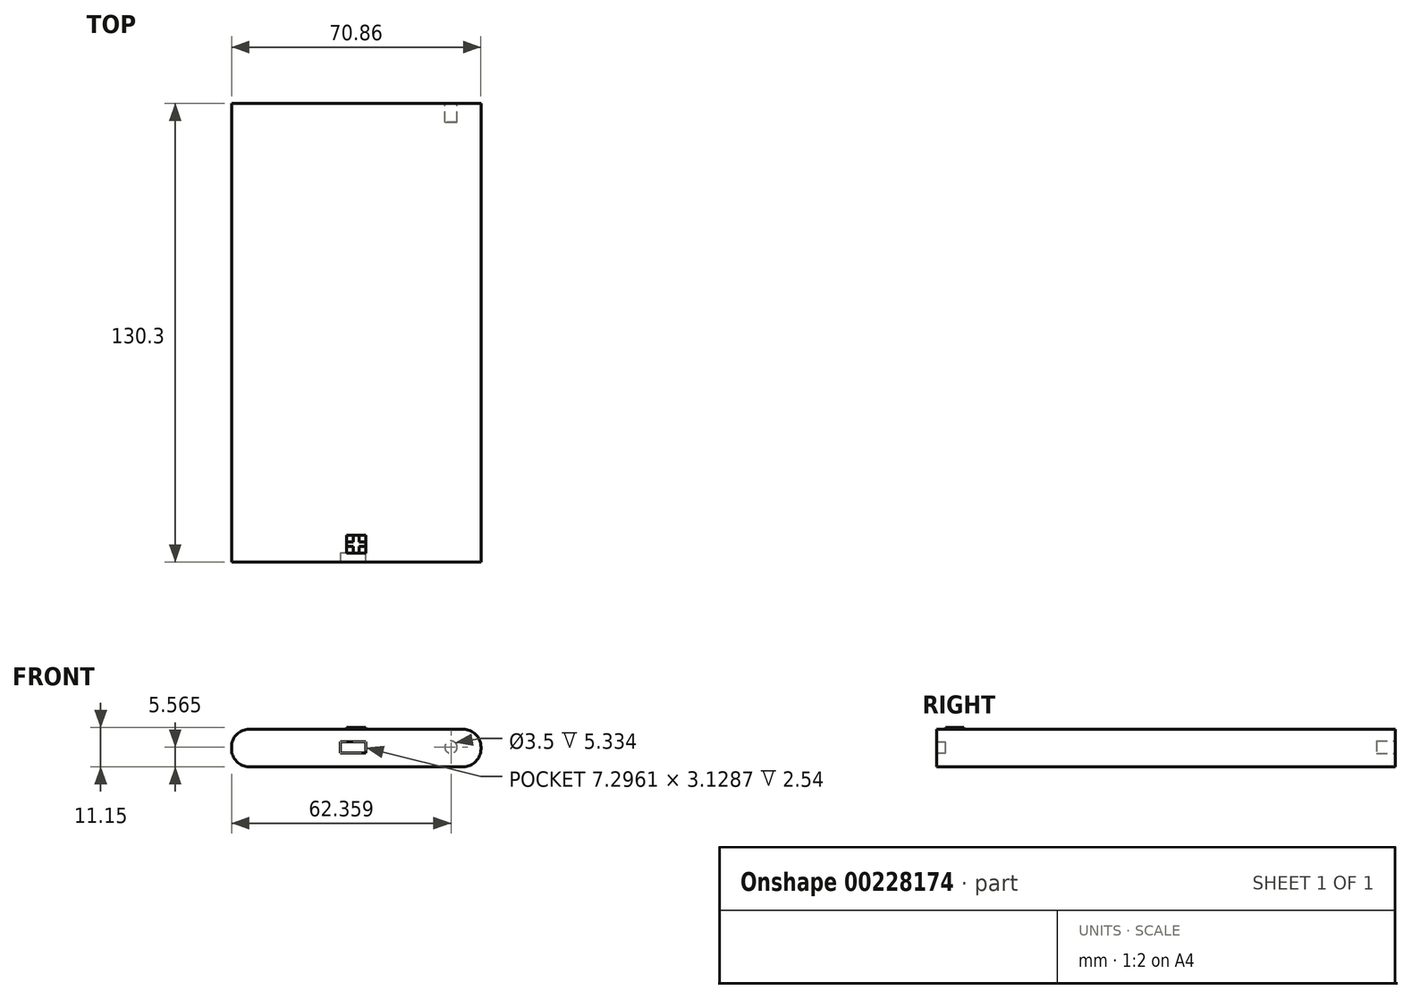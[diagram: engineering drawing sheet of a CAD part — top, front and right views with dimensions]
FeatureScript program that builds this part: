
annotation { "Feature Type Name" : "Feature", "Feature Type Description" : "" }
export const myFeature = defineFeature(function(context is Context, id is Id, definition is map)
    precondition{}
    {
        {
            var Q0;
            Q0=qCreatedBy(makeId("Top.planeOp"),FACE);
            var sketch = newSketch(context, id + "F0", { "sketchPlane" : qUnion([Q0])});
            skLineSegment(sketch, "E0.bottom", {"start": v(-84.07, 53.94) * mm, "end": v(-13.2, 53.94) * mm});
            skLineSegment(sketch, "E0.top", {"start": v(-84.07, -76.36) * mm, "end": v(-13.2, -76.36) * mm});
            skLineSegment(sketch, "E0.left", {"start": v(-84.07, 53.94) * mm, "end": v(-84.07, -76.36) * mm});
            skLineSegment(sketch, "E0.right", {"start": v(-13.2, 53.94) * mm, "end": v(-13.2, -76.36) * mm});
            skSolve(sketch);
        }
        {
            var Q0;
            Q0=makeQuery(id+"F0.imprint","IMPRINT",FACE,{"disambiguationData":[TD([[makeQuery(id+"F0.imprint","IMPRINT",EDGE,{"derivedFrom":sQuery(id+"F0.wireOp",EDGE,"E0.bottom")}),-1.0]])]});
            extrude(context, id + "F1", {"entities" : qUnion([Q0]), "depth" : 10.67 * mm});
        }
        {
            var Q0;
            Q0=makeQuery(id+"F1.opExtrude","CAP_EDGE",EDGE,{"disambiguationData":[OSD([sQuery(id+"F0.wireOp",EDGE,"E0.right")])],"isStart":false});
            var Q1;
            Q1=makeQuery(id+"F1.opExtrude","CAP_EDGE",EDGE,{"disambiguationData":[OSD([sQuery(id+"F0.wireOp",EDGE,"E0.right")])],"isStart":true});
            var Q2;
            Q2=makeQuery(id+"F1.opExtrude","CAP_EDGE",EDGE,{"disambiguationData":[OSD([sQuery(id+"F0.wireOp",EDGE,"E0.left")])],"isStart":true});
            var Q3;
            Q3=makeQuery(id+"F1.opExtrude","CAP_EDGE",EDGE,{"disambiguationData":[OSD([sQuery(id+"F0.wireOp",EDGE,"E0.left")])],"isStart":false});
            fillet(context, id + "F2", {"entities" : qUnion([Q0, Q1, Q2, Q3]), "radius" : 5.08 * mm, "tangentPropagation" : true, "allowEdgeOverflow" : false});
        }
        {
            var Q0;
            Q0=makeQuery(id+"F1.opExtrude","SWEPT_FACE",FACE,{"disambiguationData":[OSD([sQuery(id+"F0.wireOp",EDGE,"E0.top")])]});
            var sketch = newSketch(context, id + "F3", { "sketchPlane" : qUnion([Q0])});
            skLineSegment(sketch, "E1", {"start": v(-84.07, 5.59) * mm, "end": v(-9.23, 4.95) * mm, "construction": true});
            skLineSegment(sketch, "E2", {"start": v(-48.59, 5.28) * mm, "end": v(-48.68, -4.71) * mm});
            skLineSegment(sketch, "E3", {"start": v(-48.59, 5.28) * mm, "end": v(-48.59, 20.94) * mm});
            skLineSegment(sketch, "E4.bottom", {"start": v(-49.62, 7.04) * mm, "end": v(-53.17, 7.04) * mm});
            skLineSegment(sketch, "E4.top", {"start": v(-49.62, 3.9) * mm, "end": v(-53.17, 3.9) * mm});
            skLineSegment(sketch, "E4.left", {"start": v(-49.62, 7.04) * mm, "end": v(-49.62, 3.9) * mm});
            skLineSegment(sketch, "E4.right", {"start": v(-53.17, 7.04) * mm, "end": v(-53.17, 3.9) * mm});
            skLineSegment(sketch, "E5.MirrorCS", {"start": v(-48.59, 5.28) * mm, "end": v(-48.5, -4.71) * mm});
            skLineSegment(sketch, "E6.MirrorCS", {"start": v(-47.56, 7.04) * mm, "end": v(-47.56, 3.9) * mm});
            skLineSegment(sketch, "E7.MirrorCS", {"start": v(-47.56, 7.04) * mm, "end": v(-44, 7.04) * mm});
            skLineSegment(sketch, "E8.MirrorCS", {"start": v(-44, 7.04) * mm, "end": v(-44, 3.9) * mm});
            skLineSegment(sketch, "E9.MirrorCS", {"start": v(-47.56, 3.9) * mm, "end": v(-44, 3.9) * mm});
            skSolve(sketch);
        }
        {
            var Q0;
            Q0=makeQuery(id+"F3.imprint","IMPRINT",FACE,{"disambiguationData":[TD([[makeQuery(id+"F3.imprint","IMPRINT",EDGE,{"derivedFrom":sQuery(id+"F3.wireOp",EDGE,"E4.bottom")}),1.0]])]});
            var Q1;
            Q1=makeQuery(id+"F3.imprint","IMPRINT",FACE,{"disambiguationData":[TD([[makeQuery(id+"F3.imprint","IMPRINT",EDGE,{"derivedFrom":sQuery(id+"F3.wireOp",EDGE,"E6.MirrorCS")}),1.0]])]});
            extrude(context, id + "F4", {"entities" : qUnion([Q0, Q1]), "operationType" : NewBodyOperationType.REMOVE, "oppositeDirection" : true, "depth" : 2.54 * mm});
        }
        {
            var Q0;
            Q0=makeQuery(id+"F4.boolean.opBoolean","COPY",FACE,{"derivedFrom":makeQuery(id+"F4.opExtrude","SWEPT_FACE",FACE,{"disambiguationData":[OSD([sQuery(id+"F3.wireOp",EDGE,"E6.MirrorCS")])]})});
            extrude(context, id + "F5", {"entities" : qUnion([Q0]), "operationType" : NewBodyOperationType.REMOVE, "endBound" : BoundingType.UP_TO_NEXT, "oppositeDirection" : true, "depth" : 25.4 * mm});
        }
        {
            var Q0;
            Q0=makeQuery(id+"F1.opExtrude","SWEPT_FACE",FACE,{"disambiguationData":[OSD([sQuery(id+"F0.wireOp",EDGE,"E0.bottom")])]});
            var sketch = newSketch(context, id + "F6", { "sketchPlane" : qUnion([Q0])});
            skCircle(sketch, "E10", {"center": v(21.71, 5.57) * mm, "radius": 1.75 * mm});
            skSolve(sketch);
        }
        {
            var Q0;
            Q0=makeQuery(id+"F6.imprint","IMPRINT",FACE,{"disambiguationData":[TD([[makeQuery(id+"F6.imprint","IMPRINT",EDGE,{"derivedFrom":sQuery(id+"F6.wireOp",EDGE,"E10")}),1.0]])]});
            extrude(context, id + "F7", {"entities" : qUnion([Q0]), "operationType" : NewBodyOperationType.REMOVE, "oppositeDirection" : true, "depth" : 5.33 * mm});
        }
        {
            var Q0;
            {var subQ0=sQuery(id+"F3.wireOp",EDGE,"E6.MirrorCS");Q0=makeQuery(id+"F5.boolean.opBoolean","MERGE",FACE,{"derivedFrom":[makeQuery(id+"F4.boolean.opBoolean","COPY",FACE,{"derivedFrom":makeQuery(id+"F4.opExtrude","CAP_FACE",FACE,{"disambiguationData":[OSD([sQuery(id+"F3.wireOp",EDGE,"E4.bottom"),sQuery(id+"F3.wireOp",EDGE,"E4.top"),sQuery(id+"F3.wireOp",EDGE,"E4.left"),sQuery(id+"F3.wireOp",EDGE,"E4.right")])],"isStart":false})}),makeQuery(id+"F4.boolean.opBoolean","COPY",FACE,{"derivedFrom":makeQuery(id+"F4.opExtrude","CAP_FACE",FACE,{"disambiguationData":[OSD([subQ0,sQuery(id+"F3.wireOp",EDGE,"E7.MirrorCS"),sQuery(id+"F3.wireOp",EDGE,"E8.MirrorCS"),sQuery(id+"F3.wireOp",EDGE,"E9.MirrorCS")])],"isStart":false})}),makeQuery(id+"F5.opExtrude","SWEPT_FACE",FACE,{"disambiguationData":[OSD([subQ0]),TDD([makeQuery(id+"F4.boolean.opBoolean","COPY",EDGE,{"derivedFrom":makeQuery(id+"F4.opExtrude","CAP_EDGE",EDGE,{"disambiguationData":[OSD([subQ0])],"isStart":false})})])]})]});}
            var sketch = newSketch(context, id + "F8", { "sketchPlane" : qUnion([Q0])});
            skLineSegment(sketch, "E11.bottom", {"start": v(-51.3, 3.9) * mm, "end": v(-53.17, 3.9) * mm});
            skLineSegment(sketch, "E11.top", {"start": v(-51.3, 7.04) * mm, "end": v(-53.17, 7.04) * mm});
            skLineSegment(sketch, "E11.left", {"start": v(-51.3, 3.9) * mm, "end": v(-51.3, 7.04) * mm});
            skLineSegment(sketch, "E11.right", {"start": v(-53.17, 3.9) * mm, "end": v(-53.17, 7.04) * mm});
            skLineSegment(sketch, "E12", {"start": v(-48.59, 3.9) * mm, "end": v(-48.59, 10.83) * mm, "construction": true});
            skPoint(sketch, "E12.endSnap0", {"position": v(-48.59, 7.04) * mm});
            skLineSegment(sketch, "E13.MirrorCS", {"start": v(-45.88, 3.9) * mm, "end": v(-45.88, 7.04) * mm});
            skLineSegment(sketch, "E14.MirrorCS", {"start": v(-45.88, 3.9) * mm, "end": v(-44, 3.9) * mm});
            skLineSegment(sketch, "E15.MirrorCS", {"start": v(-44, 3.9) * mm, "end": v(-44, 7.04) * mm});
            skLineSegment(sketch, "E16.MirrorCS", {"start": v(-45.88, 7.04) * mm, "end": v(-44, 7.04) * mm});
            skSolve(sketch);
        }
        {
            var Q0;
            Q0=makeQuery(id+"F8.imprint","IMPRINT",FACE,{"disambiguationData":[TD([[makeQuery(id+"F8.imprint","IMPRINT",EDGE,{"derivedFrom":sQuery(id+"F8.wireOp",EDGE,"E11.bottom")}),1.0]])]});
            var Q1;
            Q1=makeQuery(id+"F8.imprint","IMPRINT",FACE,{"disambiguationData":[TD([[makeQuery(id+"F8.imprint","IMPRINT",EDGE,{"derivedFrom":sQuery(id+"F8.wireOp",EDGE,"E13.MirrorCS")}),-1.0]])]});
            var Q2;
            Q2=makeQuery(id+"F1.opExtrude","SWEPT_FACE",FACE,{"disambiguationData":[OSD([sQuery(id+"F0.wireOp",EDGE,"E0.top")])]});
            extrude(context, id + "F9", {"entities" : qUnion([Q0, Q1]), "operationType" : NewBodyOperationType.ADD, "endBound" : BoundingType.UP_TO_SURFACE, "endBoundEntityFace" : qUnion([Q2]), "depth" : 25.4 * mm});
        }
        {
            var Q0;
            Q0=makeQuery(id+"F1.opExtrude","CAP_FACE",FACE,{"disambiguationData":[OSD([sQuery(id+"F0.wireOp",EDGE,"E0.bottom"),sQuery(id+"F0.wireOp",EDGE,"E0.top"),sQuery(id+"F0.wireOp",EDGE,"E0.left"),sQuery(id+"F0.wireOp",EDGE,"E0.right")])],"isStart":false});
            var sketch = newSketch(context, id + "F10", { "sketchPlane" : qUnion([Q0])});
            skLineSegment(sketch, "E17.bottom", {"start": v(-79, -76.36) * mm, "end": v(-18.29, -76.36) * mm});
            skLineSegment(sketch, "E17.top", {"start": v(-79, -66.2) * mm, "end": v(-18.29, -66.2) * mm});
            skLineSegment(sketch, "E17.left", {"start": v(-79, -76.36) * mm, "end": v(-79, -66.2) * mm});
            skLineSegment(sketch, "E17.right", {"start": v(-18.29, -76.36) * mm, "end": v(-18.29, -66.2) * mm});
            skLineSegment(sketch, "E18", {"start": v(-48.64, -66.2) * mm, "end": v(-48.64, -76.36) * mm, "construction": true});
            skLineSegment(sketch, "E19", {"start": v(-18.29, -71.28) * mm, "end": v(-79, -71.28) * mm, "construction": true});
            skLineSegment(sketch, "E20.bottom", {"start": v(-49.46, -70.61) * mm, "end": v(-51.37, -70.61) * mm});
            skLineSegment(sketch, "E20.top", {"start": v(-49.46, -68.7) * mm, "end": v(-51.37, -68.7) * mm});
            skLineSegment(sketch, "E20.left", {"start": v(-49.46, -70.61) * mm, "end": v(-49.46, -68.7) * mm});
            skLineSegment(sketch, "E20.right", {"start": v(-51.37, -70.61) * mm, "end": v(-51.37, -68.7) * mm});
            skLineSegment(sketch, "E21.MirrorCS", {"start": v(-49.46, -71.94) * mm, "end": v(-51.37, -71.94) * mm});
            skLineSegment(sketch, "E22.MirrorCS", {"start": v(-51.37, -71.94) * mm, "end": v(-51.37, -73.85) * mm});
            skLineSegment(sketch, "E23.MirrorCS", {"start": v(-49.46, -73.85) * mm, "end": v(-51.37, -73.85) * mm});
            skLineSegment(sketch, "E24.MirrorCS", {"start": v(-49.46, -71.94) * mm, "end": v(-49.46, -73.85) * mm});
            skLineSegment(sketch, "E25.MirrorCS", {"start": v(-47.82, -68.7) * mm, "end": v(-45.91, -68.7) * mm});
            skLineSegment(sketch, "E26.MirrorCS", {"start": v(-45.91, -70.61) * mm, "end": v(-45.91, -68.7) * mm});
            skLineSegment(sketch, "E27.MirrorCS", {"start": v(-47.82, -70.61) * mm, "end": v(-45.91, -70.61) * mm});
            skLineSegment(sketch, "E28.MirrorCS", {"start": v(-47.82, -70.61) * mm, "end": v(-47.82, -68.7) * mm});
            skLineSegment(sketch, "E29.MirrorCS", {"start": v(-47.82, -73.85) * mm, "end": v(-45.91, -73.85) * mm});
            skLineSegment(sketch, "E30.MirrorCS", {"start": v(-45.91, -71.94) * mm, "end": v(-45.91, -73.85) * mm});
            skLineSegment(sketch, "E31.MirrorCS", {"start": v(-47.82, -71.94) * mm, "end": v(-45.91, -71.94) * mm});
            skLineSegment(sketch, "E32.MirrorCS", {"start": v(-47.82, -71.94) * mm, "end": v(-47.82, -73.85) * mm});
            skLineSegment(sketch, "E33.bottom", {"start": v(-51.37, -68.7) * mm, "end": v(-45.91, -68.7) * mm});
            skLineSegment(sketch, "E33.top", {"start": v(-51.37, -73.85) * mm, "end": v(-45.91, -73.85) * mm});
            skLineSegment(sketch, "E33.left", {"start": v(-51.37, -68.7) * mm, "end": v(-51.37, -73.85) * mm});
            skLineSegment(sketch, "E33.right", {"start": v(-45.91, -68.7) * mm, "end": v(-45.91, -73.85) * mm});
            skSolve(sketch);
        }
        {
            var Q0;
            {var subQ0=sQuery(id+"F10.wireOp",EDGE,"E20.bottom");Q0=makeQuery(id+"F10.imprint","IMPRINT",FACE,{"disambiguationData":[TD([[makeQuery(id+"F10.imprint","IMPRINT",EDGE,{"derivedFrom":subQ0}),-1.0]])]});}
            var Q1;
            {var subQ0=sQuery(id+"F10.wireOp",EDGE,"E21.MirrorCS");Q1=makeQuery(id+"F10.imprint","IMPRINT",FACE,{"disambiguationData":[TD([[makeQuery(id+"F10.imprint","IMPRINT",EDGE,{"derivedFrom":subQ0}),1.0]])]});}
            var Q2;
            {var subQ0=sQuery(id+"F10.wireOp",EDGE,"E31.MirrorCS");Q2=makeQuery(id+"F10.imprint","IMPRINT",FACE,{"disambiguationData":[TD([[makeQuery(id+"F10.imprint","IMPRINT",EDGE,{"derivedFrom":subQ0}),-1.0]])]});}
            var Q3;
            {var subQ0=sQuery(id+"F10.wireOp",EDGE,"E27.MirrorCS");Q3=makeQuery(id+"F10.imprint","IMPRINT",FACE,{"disambiguationData":[TD([[makeQuery(id+"F10.imprint","IMPRINT",EDGE,{"derivedFrom":subQ0}),1.0]])]});}
            extrude(context, id + "F11", {"entities" : qUnion([Q0, Q1, Q2, Q3]), "operationType" : NewBodyOperationType.ADD, "depth" : 0.25 * mm});
        }
        {
            var Q0;
            {var subQ6=sQuery(id+"F10.wireOp",EDGE,"E20.bottom");Q0=makeQuery(id+"F10.imprint","IMPRINT",FACE,{"disambiguationData":[TD([[makeQuery(id+"F10.imprint","IMPRINT",EDGE,{"derivedFrom":subQ6}),1.0]])]});}
            extrude(context, id + "F12", {"entities" : qUnion([Q0]), "operationType" : NewBodyOperationType.ADD, "depth" : 0.48 * mm});
        }
    });
